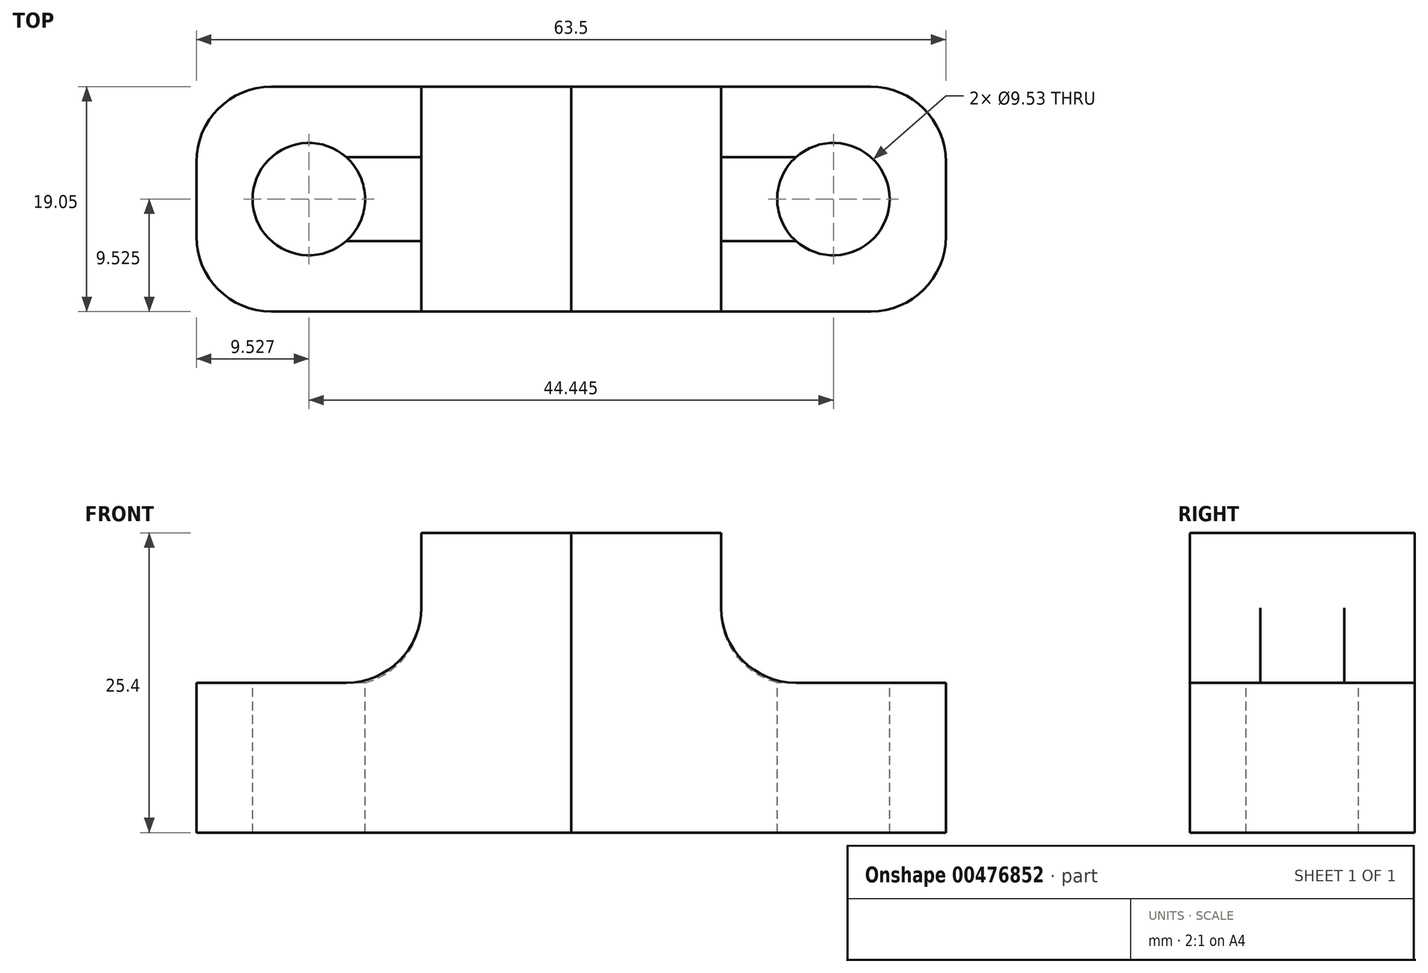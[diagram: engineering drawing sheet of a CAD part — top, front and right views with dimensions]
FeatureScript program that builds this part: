
annotation { "Feature Type Name" : "Feature", "Feature Type Description" : "" }
export const myFeature = defineFeature(function(context is Context, id is Id, definition is map)
    precondition{}
    {
        {
            var Q0;
            Q0=qCreatedBy(makeId("Front.planeOp"),FACE);
            var sketch = newSketch(context, id + "F0", { "sketchPlane" : qUnion([Q0])});
            skLineSegment(sketch, "E0", {"start": v(0, 12.7) * mm, "end": v(0, -12.7) * mm});
            skLineSegment(sketch, "E1", {"start": v(0, 12.7) * mm, "end": v(-12.7, 12.7) * mm});
            skLineSegment(sketch, "E2", {"start": v(-12.7, 12.7) * mm, "end": v(-12.7, 0) * mm});
            skLineSegment(sketch, "E3", {"start": v(-12.7, 0) * mm, "end": v(-31.75, 0) * mm});
            skLineSegment(sketch, "E4", {"start": v(-31.75, 0) * mm, "end": v(-31.75, -12.7) * mm});
            skLineSegment(sketch, "E5", {"start": v(-31.75, -12.7) * mm, "end": v(0, -12.7) * mm});
            skSolve(sketch);
        }
        {
            var Q0;
            Q0=makeQuery(id+"F0.imprint","IMPRINT",FACE,{"disambiguationData":[TD([[makeQuery(id+"F0.imprint","IMPRINT",EDGE,{"derivedFrom":sQuery(id+"F0.wireOp",EDGE,"E0")}),-1.0]])]});
            extrude(context, id + "F1", {"entities" : qUnion([Q0]), "depth" : 19.05 * mm});
        }
        {
            var Q0;
            Q0=makeQuery(id+"F1.opExtrude","SWEPT_FACE",FACE,{"disambiguationData":[OSD([sQuery(id+"F0.wireOp",EDGE,"E3")])]});
            var sketch = newSketch(context, id + "F2", { "sketchPlane" : qUnion([Q0])});
            skCircle(sketch, "E6", {"center": v(-22.22, -9.53) * mm, "radius": 4.76 * mm});
            skPoint(sketch, "E6.centerSnap0", {"position": v(-22.22, -19.05) * mm});
            skPoint(sketch, "E6.centerSnap1", {"position": v(-31.75, -9.53) * mm});
            skSolve(sketch);
        }
        {
            var Q0;
            Q0=makeQuery(id+"F2.imprint","IMPRINT",FACE,{"disambiguationData":[TD([[makeQuery(id+"F2.imprint","IMPRINT",EDGE,{"derivedFrom":sQuery(id+"F2.wireOp",EDGE,"E6")}),1.0]])]});
            extrude(context, id + "F3", {"entities" : qUnion([Q0]), "operationType" : NewBodyOperationType.REMOVE, "oppositeDirection" : true, "depth" : 25.4 * mm});
        }
        {
            var Q0;
            Q0=makeQuery(id+"F1.opExtrude","CAP_EDGE",EDGE,{"disambiguationData":[OSD([sQuery(id+"F0.wireOp",EDGE,"E4")])],"isStart":false});
            var Q1;
            Q1=makeQuery(id+"F1.opExtrude","CAP_EDGE",EDGE,{"disambiguationData":[OSD([sQuery(id+"F0.wireOp",EDGE,"E4")])],"isStart":true});
            var Q2;
            Q2=makeQuery(id+"F1.opExtrude","SWEPT_EDGE",EDGE,{"disambiguationData":[OSD([sQuery(id+"F0.wireOp",EDGE,"E2"),sQuery(id+"F0.wireOp",EDGE,"E3")])]});
            fillet(context, id + "F4", {"entities" : qUnion([Q0, Q1, Q2]), "radius" : 6.35 * mm, "tangentPropagation" : true, "allowEdgeOverflow" : false});
        }
        {
            var Q0;
            Q0=makeQuery(id+"F1.opExtrude","SWEPT_BODY",BODY,{"disambiguationData":[OSD([sQuery(id+"F0.wireOp",EDGE,"E0"),sQuery(id+"F0.wireOp",EDGE,"E1"),sQuery(id+"F0.wireOp",EDGE,"E2"),sQuery(id+"F0.wireOp",EDGE,"E3"),sQuery(id+"F0.wireOp",EDGE,"E4"),sQuery(id+"F0.wireOp",EDGE,"E5")])]});
            var Q1;
            Q1=qCreatedBy(makeId("Right.planeOp"),FACE);
            mirror(context, id + "F5", {"entities" : qUnion([Q0]), "mirrorPlane" : qUnion([Q1])});
        }
    });
